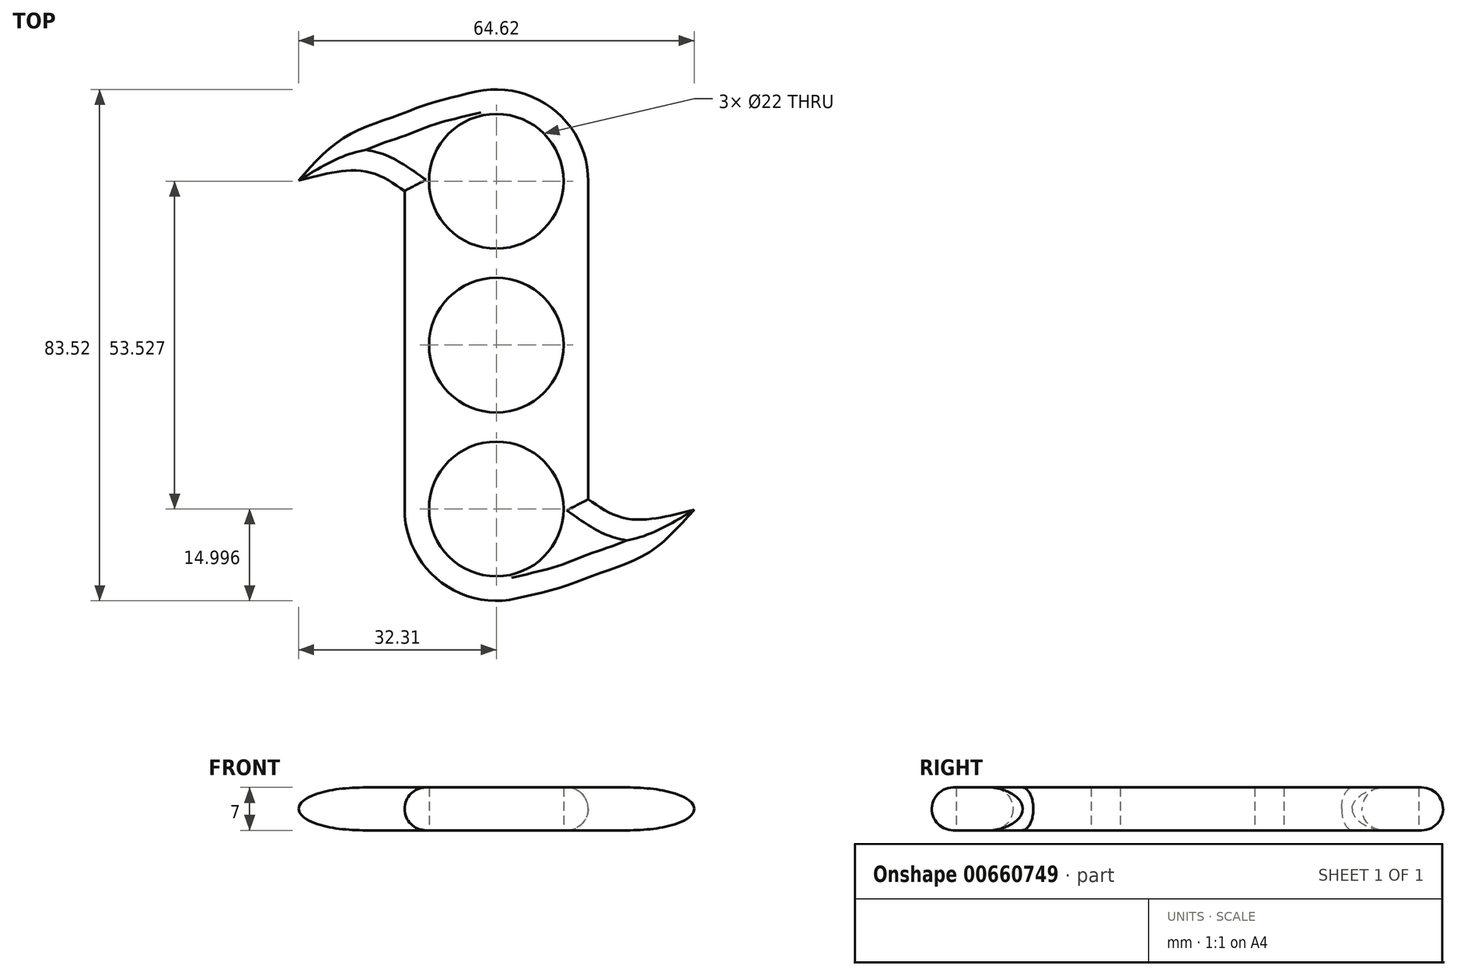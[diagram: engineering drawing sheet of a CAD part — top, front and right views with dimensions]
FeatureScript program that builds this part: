
annotation { "Feature Type Name" : "Feature", "Feature Type Description" : "" }
export const myFeature = defineFeature(function(context is Context, id is Id, definition is map)
    precondition{}
    {
        {
            var Q0;
            Q0=qCreatedBy(makeId("Top.planeOp"),FACE);
            var sketch = newSketch(context, id + "F0", { "sketchPlane" : qUnion([Q0])});
            skCircle(sketch, "E0", {"center": v(0, 0) * mm, "radius": 11 * mm});
            skLineSegment(sketch, "E1", {"start": v(0, 0) * mm, "end": v(0, 26.76) * mm});
            skCircle(sketch, "E2", {"center": v(0, 26.76) * mm, "radius": 11 * mm});
            skArc(sketch, "E3", {"start": v(15, 26.76) * mm, "mid": v(0, 41.76) * mm, "end": v(-15, 26.76) * mm});
            skArc(sketch, "E4", {"start": v(-15, 0) * mm, "mid": v(0, -15) * mm, "end": v(15, 0) * mm});
            skLineSegment(sketch, "E5", {"start": v(-15, 26.76) * mm, "end": v(-15, 0) * mm});
            skLineSegment(sketch, "E6", {"start": v(15, 26.76) * mm, "end": v(15, 0) * mm});
            skArc(sketch, "E7.1.0", {"start": v(-15, -26.76) * mm, "mid": v(0, -41.76) * mm, "end": v(15, -26.76) * mm});
            skLineSegment(sketch, "E7.1.1", {"start": v(15, -26.76) * mm, "end": v(15, 0) * mm});
            skLineSegment(sketch, "E7.1.2", {"start": v(-15, -26.76) * mm, "end": v(-15, 0) * mm});
            skCircle(sketch, "E7.1.3", {"center": v(0, -26.76) * mm, "radius": 11 * mm});
            skArc(sketch, "E7.1.5", {"start": v(15, 0) * mm, "mid": v(0, 15) * mm, "end": v(-15, 0) * mm});
            skFitSpline(sketch, "E8", {"points": [v(-32.31, 26.9) * mm, v(-24.45, 34.15) * mm, v(-16.22, 37.47) * mm, v(-11.43, 39.31) * mm, v(-0.5, 42.02) * mm], "startDerivative": vector(26.47, 29.7) * mm, "endDerivative": vector(43.56, 9.56) * mm});
            skFitSpline(sketch, "E9", {"points": [v(-32.31, 26.9) * mm, v(-21.5, 28.38) * mm, v(-15, 25.19) * mm], "startDerivative": vector(21.04, 5.37) * mm, "endDerivative": vector(13.32, -9.31) * mm});
            skFitSpline(sketch, "E10.MirrorCS", {"points": [v(32.31, -26.9) * mm, v(24.45, -34.15) * mm, v(16.22, -37.47) * mm, v(11.43, -39.31) * mm, v(0.5, -42.02) * mm], "startDerivative": vector(-26.47, -29.7) * mm, "endDerivative": vector(-43.56, -9.56) * mm});
            skFitSpline(sketch, "E11.MirrorCS", {"points": [v(32.31, -26.9) * mm, v(21.5, -28.38) * mm, v(15, -25.19) * mm], "startDerivative": vector(-21.04, -5.37) * mm, "endDerivative": vector(-13.32, 9.31) * mm});
            skPoint(sketch, "E12.MirrorCS.end.orphan", {"position": v(-15, -25.19) * mm});
            skPoint(sketch, "E12.MirrorCS.start.orphan", {"position": v(-32.31, -26.9) * mm});
            skPoint(sketch, "E13.MirrorCS.end.orphan", {"position": v(-0.5, -42.02) * mm});
            skSolve(sketch);
        }
        {
            var Q0;
            Q0=makeQuery(id+"F0.imprint","IMPRINT",FACE,{"disambiguationData":[TD([[makeQuery(id+"F0.imprint","IMPRINT",EDGE,{"derivedFrom":sQuery(id+"F0.wireOp",EDGE,"E2")}),-1.0]])]});
            var Q1;
            {var subQ1=sQuery(id+"F0.wireOp",EDGE,"E4");Q1=makeQuery(id+"F0.imprint","IMPRINT",FACE,{"disambiguationData":[TD([[makeQuery(id+"F0.imprint","IMPRINT",EDGE,{"derivedFrom":subQ1}),-1.0]])]});}
            var Q2;
            {var subQ0=sQuery(id+"F0.wireOp",EDGE,"E4");Q2=makeQuery(id+"F0.imprint","IMPRINT",FACE,{"disambiguationData":[TD([[makeQuery(id+"F0.imprint","IMPRINT",EDGE,{"derivedFrom":subQ0}),1.0]])]});}
            var Q3;
            {var subQ3=sQuery(id+"F0.wireOp",EDGE,"E8");Q3=makeQuery(id+"F0.imprint","IMPRINT",FACE,{"disambiguationData":[TD([[makeQuery(id+"F0.imprint","IMPRINT",EDGE,{"derivedFrom":subQ3}),-1.0]])]});}
            var Q4;
            {var subQ3=sQuery(id+"F0.wireOp",EDGE,"E10.MirrorCS");Q4=makeQuery(id+"F0.imprint","IMPRINT",FACE,{"disambiguationData":[TD([[makeQuery(id+"F0.imprint","IMPRINT",EDGE,{"derivedFrom":subQ3}),-1.0]])]});}
            extrude(context, id + "F1", {"entities" : qUnion([Q0, Q1, Q2, Q3, Q4]), "depth" : 7 * mm, "offsetDistance" : 25 * mm});
        }
        {
            var Q0;
            Q0=makeQuery(id+"F1.opExtrude","CAP_EDGE",EDGE,{"disambiguationData":[OSD([sQuery(id+"F0.wireOp",EDGE,"E3")])],"isStart":false});
            var Q1;
            Q1=makeQuery(id+"F1.opExtrude","CAP_EDGE",EDGE,{"disambiguationData":[OSD([sQuery(id+"F0.wireOp",EDGE,"E3")])],"isStart":true});
            var Q2;
            Q2=makeQuery(id+"F1.opExtrude","CAP_EDGE",EDGE,{"disambiguationData":[OSD([sQuery(id+"F0.wireOp",EDGE,"E5"),sQuery(id+"F0.wireOp",EDGE,"E7.1.2")])],"isStart":false});
            var Q3;
            Q3=makeQuery(id+"F1.opExtrude","CAP_EDGE",EDGE,{"disambiguationData":[OSD([sQuery(id+"F0.wireOp",EDGE,"E5"),sQuery(id+"F0.wireOp",EDGE,"E7.1.2")])],"isStart":true});
            var Q4;
            Q4=makeQuery(id+"F1.opExtrude","CAP_EDGE",EDGE,{"disambiguationData":[OSD([sQuery(id+"F0.wireOp",EDGE,"E6"),sQuery(id+"F0.wireOp",EDGE,"E7.1.1")])],"isStart":true});
            var Q5;
            Q5=makeQuery(id+"F1.opExtrude","CAP_EDGE",EDGE,{"disambiguationData":[OSD([sQuery(id+"F0.wireOp",EDGE,"E6"),sQuery(id+"F0.wireOp",EDGE,"E7.1.1")])],"isStart":false});
            var Q6;
            Q6=makeQuery(id+"F1.opExtrude","CAP_EDGE",EDGE,{"disambiguationData":[OSD([sQuery(id+"F0.wireOp",EDGE,"E7.1.0")])],"isStart":true});
            var Q7;
            Q7=makeQuery(id+"F1.opExtrude","CAP_EDGE",EDGE,{"disambiguationData":[OSD([sQuery(id+"F0.wireOp",EDGE,"E7.1.0")])],"isStart":false});
            var Q8;
            Q8=makeQuery(id+"F1.opExtrude","CAP_EDGE",EDGE,{"disambiguationData":[OSD([sQuery(id+"F0.wireOp",EDGE,"E9")])],"isStart":false});
            var Q9;
            Q9=makeQuery(id+"F1.opExtrude","CAP_EDGE",EDGE,{"disambiguationData":[OSD([sQuery(id+"F0.wireOp",EDGE,"E9")])],"isStart":true});
            var Q10;
            Q10=makeQuery(id+"F1.opExtrude","CAP_EDGE",EDGE,{"disambiguationData":[OSD([sQuery(id+"F0.wireOp",EDGE,"E11.MirrorCS")])],"isStart":true});
            var Q11;
            Q11=makeQuery(id+"F1.opExtrude","CAP_EDGE",EDGE,{"disambiguationData":[OSD([sQuery(id+"F0.wireOp",EDGE,"E11.MirrorCS")])],"isStart":false});
            fillet(context, id + "F2", {"entities" : qUnion([Q0, Q1, Q2, Q3, Q4, Q5, Q6, Q7, Q8, Q9, Q10, Q11]), "radius" : 3.5 * mm, "tangentPropagation" : true, "allowEdgeOverflow" : false});
        }
    });
